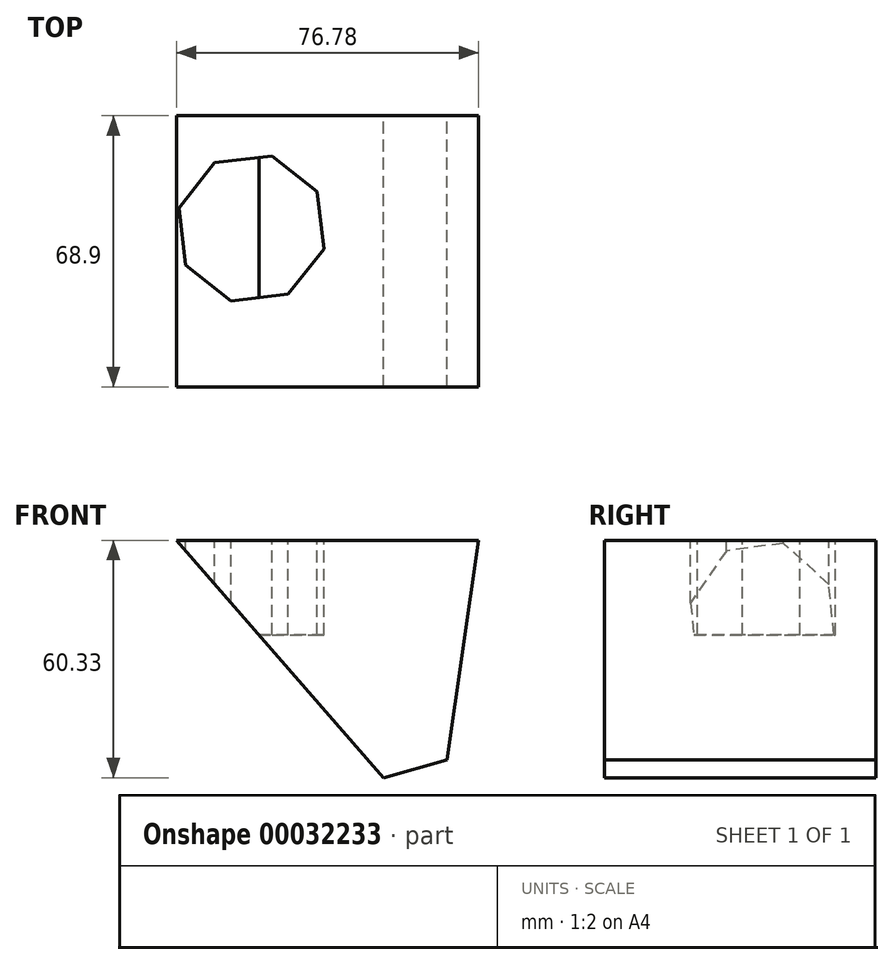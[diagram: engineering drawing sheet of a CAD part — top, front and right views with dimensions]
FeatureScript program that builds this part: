
annotation { "Feature Type Name" : "Feature", "Feature Type Description" : "" }
export const myFeature = defineFeature(function(context is Context, id is Id, definition is map)
    precondition{}
    {
        {
            var Q0;
            Q0=qCreatedBy(makeId("Front.planeOp"),FACE);
            var sketch = newSketch(context, id + "F0", { "sketchPlane" : qUnion([Q0])});
            skLineSegment(sketch, "E0", {"start": v(-52.63, 60.33) * mm, "end": v(24.15, 60.33) * mm});
            skLineSegment(sketch, "E1", {"start": v(24.15, 60.33) * mm, "end": v(16.05, 4.5) * mm});
            skLineSegment(sketch, "E2", {"start": v(16.05, 4.5) * mm, "end": v(0, 0) * mm});
            skLineSegment(sketch, "E3", {"start": v(0, 0) * mm, "end": v(-52.63, 60.33) * mm});
            skSolve(sketch);
        }
        {
            var Q0;
            Q0=makeQuery(id+"F0.imprint","IMPRINT",FACE,{"disambiguationData":[TD([[makeQuery(id+"F0.imprint","IMPRINT",EDGE,{"derivedFrom":sQuery(id+"F0.wireOp",EDGE,"E0")}),-1.0]])]});
            extrude(context, id + "F1", {"entities" : qUnion([Q0]), "depth" : 68.9 * mm});
        }
        {
            var Q0;
            Q0=makeQuery(id+"F1.opExtrude","SWEPT_FACE",FACE,{"disambiguationData":[OSD([sQuery(id+"F0.wireOp",EDGE,"E0")])]});
            var sketch = newSketch(context, id + "F2", { "sketchPlane" : qUnion([Q0])});
            skCircle(sketch, "E4.cCircle", {"center": v(-33.58, -28.65) * mm, "radius": 17.7 * mm, "construction": true});
            skLineSegment(sketch, "E4.0", {"start": v(-15.16, -33.87) * mm, "end": v(-24.25, -45.37) * mm});
            skLineSegment(sketch, "E4.1", {"start": v(-24.25, -45.37) * mm, "end": v(-38.8, -47.07) * mm});
            skLineSegment(sketch, "E4.2", {"start": v(-38.8, -47.07) * mm, "end": v(-50.3, -37.98) * mm});
            skLineSegment(sketch, "E4.3", {"start": v(-50.3, -37.98) * mm, "end": v(-52, -23.42) * mm});
            skLineSegment(sketch, "E4.4", {"start": v(-52, -23.42) * mm, "end": v(-42.9, -11.92) * mm});
            skLineSegment(sketch, "E4.5", {"start": v(-42.9, -11.92) * mm, "end": v(-28.35, -10.23) * mm});
            skLineSegment(sketch, "E4.6", {"start": v(-28.35, -10.23) * mm, "end": v(-16.86, -19.32) * mm});
            skLineSegment(sketch, "E4.7", {"start": v(-16.86, -19.32) * mm, "end": v(-15.16, -33.87) * mm});
            skPoint(sketch, "E4.0.midPoint", {"position": v(-19.7, -39.62) * mm});
            skSolve(sketch);
        }
        {
            var Q0;
            Q0=makeQuery(id+"F2.imprint","IMPRINT",FACE,{"disambiguationData":[TD([[makeQuery(id+"F2.imprint","IMPRINT",EDGE,{"derivedFrom":sQuery(id+"F2.wireOp",EDGE,"E4.0")}),-1.0]])]});
            extrude(context, id + "F3", {"entities" : qUnion([Q0]), "operationType" : NewBodyOperationType.REMOVE, "oppositeDirection" : true, "depth" : 24 * mm});
        }
    });
